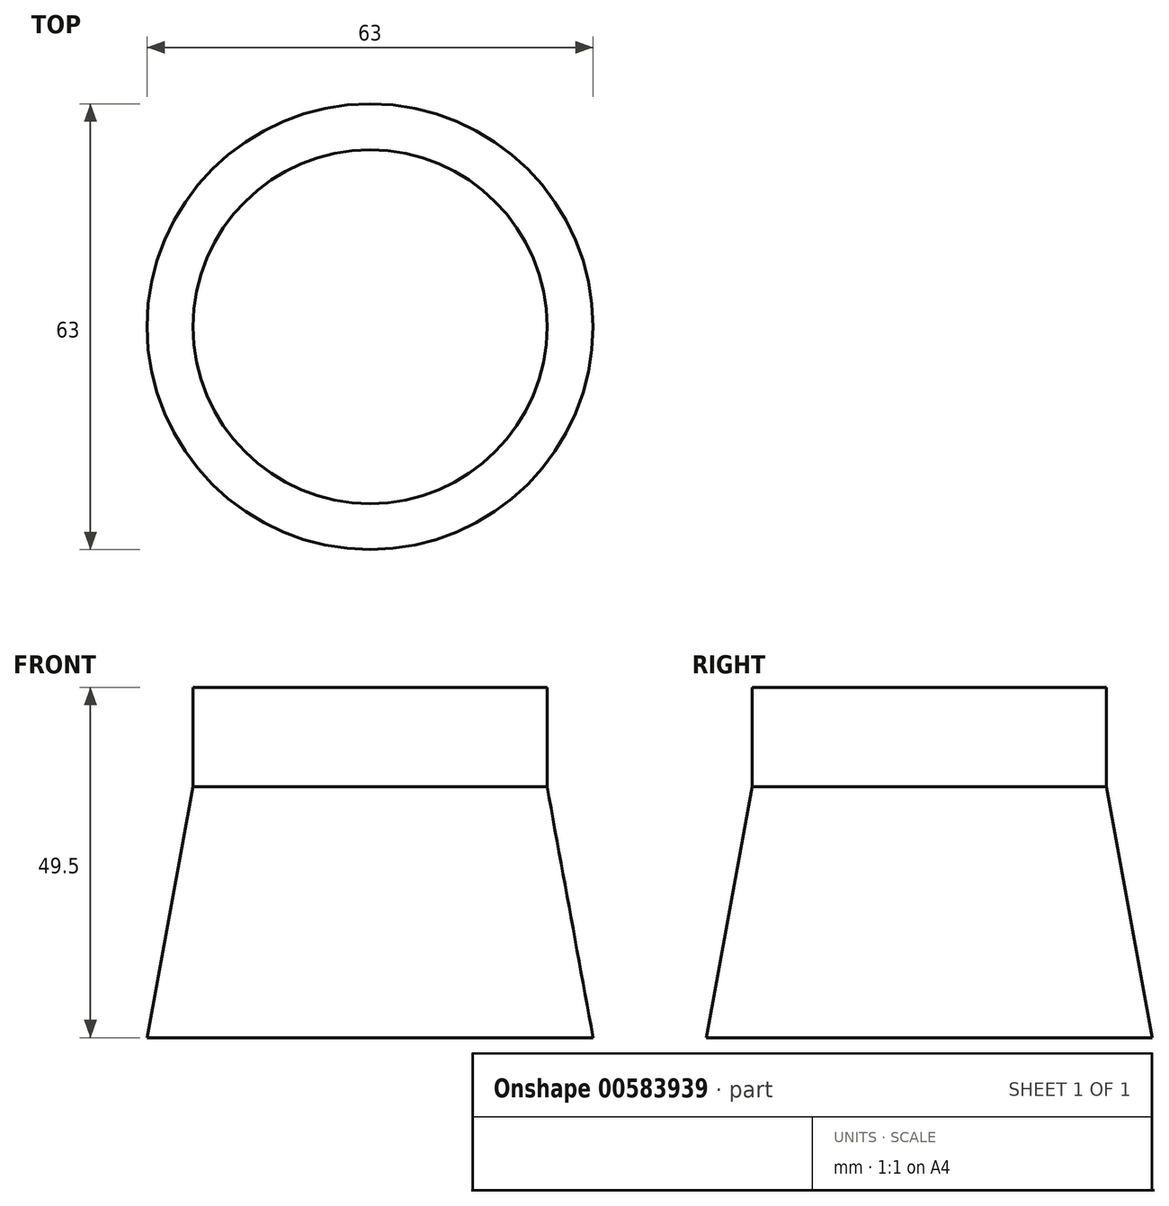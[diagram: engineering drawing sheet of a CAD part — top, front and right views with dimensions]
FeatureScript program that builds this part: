
annotation { "Feature Type Name" : "Feature", "Feature Type Description" : "" }
export const myFeature = defineFeature(function(context is Context, id is Id, definition is map)
    precondition{}
    {
        {
            var Q0;
            Q0=qCreatedBy(makeId("Top.planeOp"),FACE);
            var sketch = newSketch(context, id + "F0", { "sketchPlane" : qUnion([Q0])});
            skCircle(sketch, "E0", {"center": v(0, 0) * mm, "radius": 31.5 * mm});
            skSolve(sketch);
        }
        {
            var Q0;
            Q0=qCreatedBy(makeId("Top.planeOp"),FACE);
            cPlane(context, id + "F1", {"entities" : qUnion([Q0]), "cplaneType" : CPlaneType.OFFSET, "offset" : 35.5 * mm, "width" : 150 * mm, "height" : 150 * mm});
        }
        {
            var Q0;
            Q0=qCreatedBy(id+"F1.planeOp",FACE);
            var sketch = newSketch(context, id + "F2", { "sketchPlane" : qUnion([Q0])});
            skCircle(sketch, "E1", {"center": v(0, 0) * mm, "radius": 25 * mm});
            skSolve(sketch);
        }
        {
            var Q0;
            Q0=makeQuery(id+"F0.imprint","IMPRINT",FACE,{"disambiguationData":[TD([[makeQuery(id+"F0.imprint","IMPRINT",EDGE,{"derivedFrom":sQuery(id+"F0.wireOp",EDGE,"E0")}),1.0]])]});
            var Q1;
            Q1=makeQuery(id+"F2.imprint","IMPRINT",FACE,{"disambiguationData":[TD([[makeQuery(id+"F2.imprint","IMPRINT",EDGE,{"derivedFrom":sQuery(id+"F2.wireOp",EDGE,"E1")}),1.0]])]});
            loft(context, id + "F3", {"sheetProfilesArray" : [{ "sheetProfileEntities" : qUnion([Q0]) }, { "sheetProfileEntities" : qUnion([Q1]) }]});
        }
        {
            var Q0;
            Q0=makeQuery(id+"F3.opLoft","CAP_FACE",FACE,{"disambiguationData":[OSD([makeQuery(id+"F2.imprint","IMPRINT",FACE,{"disambiguationData":[TD([[makeQuery(id+"F2.imprint","IMPRINT",EDGE,{"derivedFrom":sQuery(id+"F2.wireOp",EDGE,"E1")}),1.0]])]})])],"isStart":true});
            extrude(context, id + "F4", {"entities" : qUnion([Q0]), "depth" : 14 * mm, "offsetDistance" : 25 * mm});
        }
    });
